# Revit family: Sidewall-Propeller-Fan_LZDK_K-Series-Direct-Drive_Carnes
name_source: partatom
category: Mechanical Equipment
revit_build: Autodesk Revit Architecture 2012 (Build: 20110916_2132(x64)
units: mm (PartAtom-declared; Revit-internal decimal feet)

## types (6) — shared parameters
04 CSI = 23 34 23
95 CSI = 15830
Assembly Code = D3040200
Catalog URL = http://www.carnes.com
Description = K Series Direct Drive SideWall Propeller Fans
E = 1 1/2"
Housing = Aluminum-Carnes-Spun-Brushed
IOM Instructions URL = http://www.carnes.com
Manufacturer = Carnes Company
Manufacturer Fax = 608-845-6470
Parts List URL = http://www.carnes.com
Product Page URL = http://www.carnes.com
Subcategory = Spun Aluminum Exhausters
URL = http://www.carnes.com
Warranty URL = http://www.carnes.com
ecoScorecard Product Page = http://ecoscorecard.com

## per-type parameters (varying)
| type | A | Blade Diameter | Blade Radius | C | F Diameter | F Radius |
| LZDK 9-10 | 16" | 9 3/4" | 3 1/8" | 10" | 10 1/4" | 5 1/8" |
| LZDK 11-12 | 16" | 11 3/4" | 4 1/8" | 10" | 12 1/4" | 6 1/8" |
| LZDK 13-14 | 20" | 13 3/4" | 5 1/8" | 11" | 14 1/4" | 7 1/8" |
| LZDK 15-16 | 20" | 15 3/4" | 6 1/8" | 12" | 16 1/4" | 8 1/8" |
| LZDK 17-18 | 24" | 17 3/4" | 7 1/8" | 12" | 18 1/4" | 9 1/8" |
| LZDK 19-21 | 24" | 19 3/4" | 8 1/8" | 12" | 20 1/4" | 10 1/8" |

note: column(s) folded — value = type name in every type: Model

## geometry (parser evidence)
native form markers: Blend x4, Sweep x5
no freeform markers — native parametric forms only
